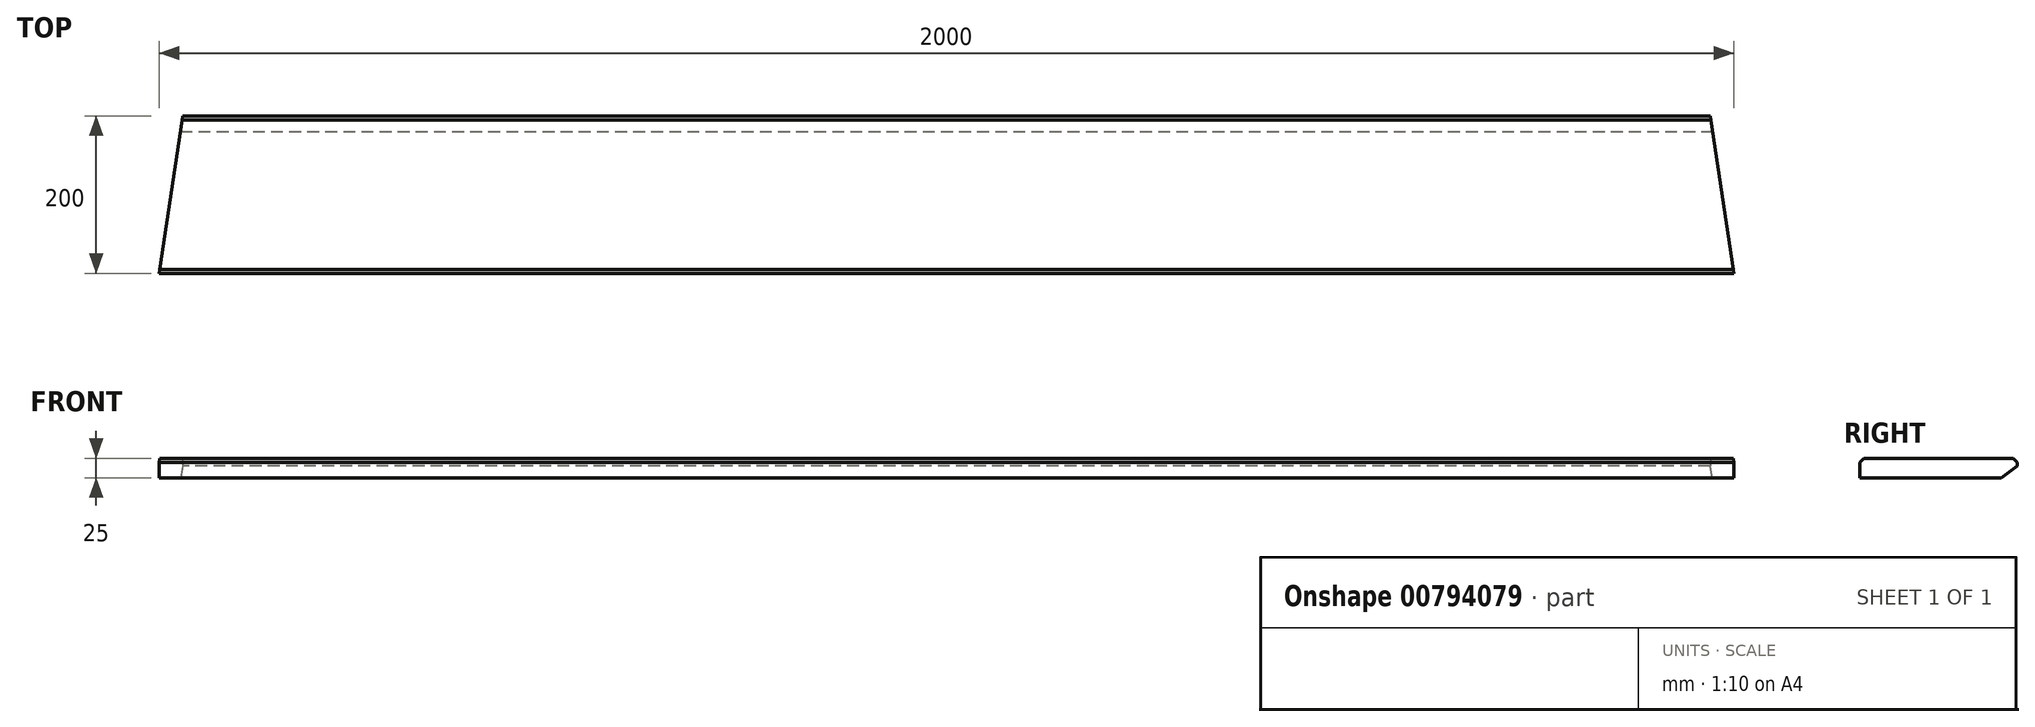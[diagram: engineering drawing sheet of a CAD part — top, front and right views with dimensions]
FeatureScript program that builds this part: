
annotation { "Feature Type Name" : "Feature", "Feature Type Description" : "" }
export const myFeature = defineFeature(function(context is Context, id is Id, definition is map)
    precondition{}
    {
        {
            var Q0;
            Q0=qCreatedBy(makeId("Front.planeOp"),FACE);
            var sketch = newSketch(context, id + "F0", { "sketchPlane" : qUnion([Q0])});
            skLineSegment(sketch, "E0.bottom", {"start": v(0, 0) * mm, "end": v(-2000, 0) * mm});
            skLineSegment(sketch, "E0.top", {"start": v(0, 25) * mm, "end": v(-2000, 25) * mm});
            skLineSegment(sketch, "E0.left", {"start": v(0, 0) * mm, "end": v(0, 25) * mm});
            skLineSegment(sketch, "E0.right", {"start": v(-2000, 0) * mm, "end": v(-2000, 25) * mm});
            skSolve(sketch);
        }
        {
            var Q0;
            Q0 = qSketchRegion(id + "F0", true);
            extrude(context, id + "F1", {"entities" : qUnion([Q0]), "depth" : 200 * mm, "offsetDistance" : 25 * mm});
        }
        {
            var Q0;
            Q0=makeQuery(id+"F1.opExtrude","CAP_EDGE",EDGE,{"disambiguationData":[OSD([sQuery(id+"F0.wireOp",EDGE,"E0.top")])],"isStart":false});
            var Q1;
            Q1=makeQuery(id+"F1.opExtrude","CAP_EDGE",EDGE,{"disambiguationData":[OSD([sQuery(id+"F0.wireOp",EDGE,"E0.top")])],"isStart":true});
            chamfer(context, id + "F2", {"entities" : qUnion([Q0, Q1]), "width" : 5 * mm, "tangentPropagation" : true});
        }
        {
            var Q0;
            Q0=qCreatedBy(makeId("Top.planeOp"),FACE);
            var sketch = newSketch(context, id + "F3", { "sketchPlane" : qUnion([Q0])});
            skLineSegment(sketch, "E1", {"start": v(0, 0) * mm, "end": v(-30, 0) * mm});
            skLineSegment(sketch, "E2", {"start": v(-1000, 0) * mm, "end": v(-1000, -58.08) * mm, "construction": true});
            skLineSegment(sketch, "E3", {"start": v(0, 0) * mm, "end": v(0, -200) * mm});
            skLineSegment(sketch, "E4", {"start": v(0, -200) * mm, "end": v(-30, 0) * mm});
            skLineSegment(sketch, "E5", {"start": v(-30, 0) * mm, "end": v(0, 0) * mm});
            skLineSegment(sketch, "E6.MirrorCS", {"start": v(-2000, -200) * mm, "end": v(-1970, 0) * mm});
            skLineSegment(sketch, "E7.MirrorCS", {"start": v(-2000, 0) * mm, "end": v(-2000, -200) * mm});
            skLineSegment(sketch, "E8.MirrorCS", {"start": v(-1970, 0) * mm, "end": v(-2000, 0) * mm});
            skSolve(sketch);
        }
        {
            var Q0;
            Q0 = qSketchRegion(id + "F3", true);
            extrude(context, id + "F4", {"entities" : qUnion([Q0]), "operationType" : NewBodyOperationType.REMOVE, "depth" : 153 * mm, "offsetDistance" : 25 * mm});
        }
        {
            var Q0;
            Q0=makeQuery(id+"F1.opExtrude","CAP_EDGE",EDGE,{"disambiguationData":[OSD([sQuery(id+"F0.wireOp",EDGE,"E0.bottom")])],"isStart":true});
            var Q1;
            Q1=makeQuery(id+"F4.boolean.opBoolean","COPY",EDGE,{"derivedFrom":makeQuery(id+"F4.opExtrude","CAP_EDGE",EDGE,{"disambiguationData":[OSD([sQuery(id+"F3.wireOp",EDGE,"E4")])],"isStart":true})});
            var Q2;
            Q2=makeQuery(id+"F4.boolean.opBoolean","COPY",EDGE,{"derivedFrom":makeQuery(id+"F4.opExtrude","CAP_EDGE",EDGE,{"disambiguationData":[OSD([sQuery(id+"F3.wireOp",EDGE,"E6.MirrorCS")])],"isStart":true})});
            chamfer(context, id + "F5", {"entities" : qUnion([Q0, Q1, Q2]), "chamferType" : ChamferType.TWO_OFFSETS, "width1" : 15 * mm, "oppositeDirection" : false, "width2" : 20 * mm, "tangentPropagation" : true});
        }
    });
